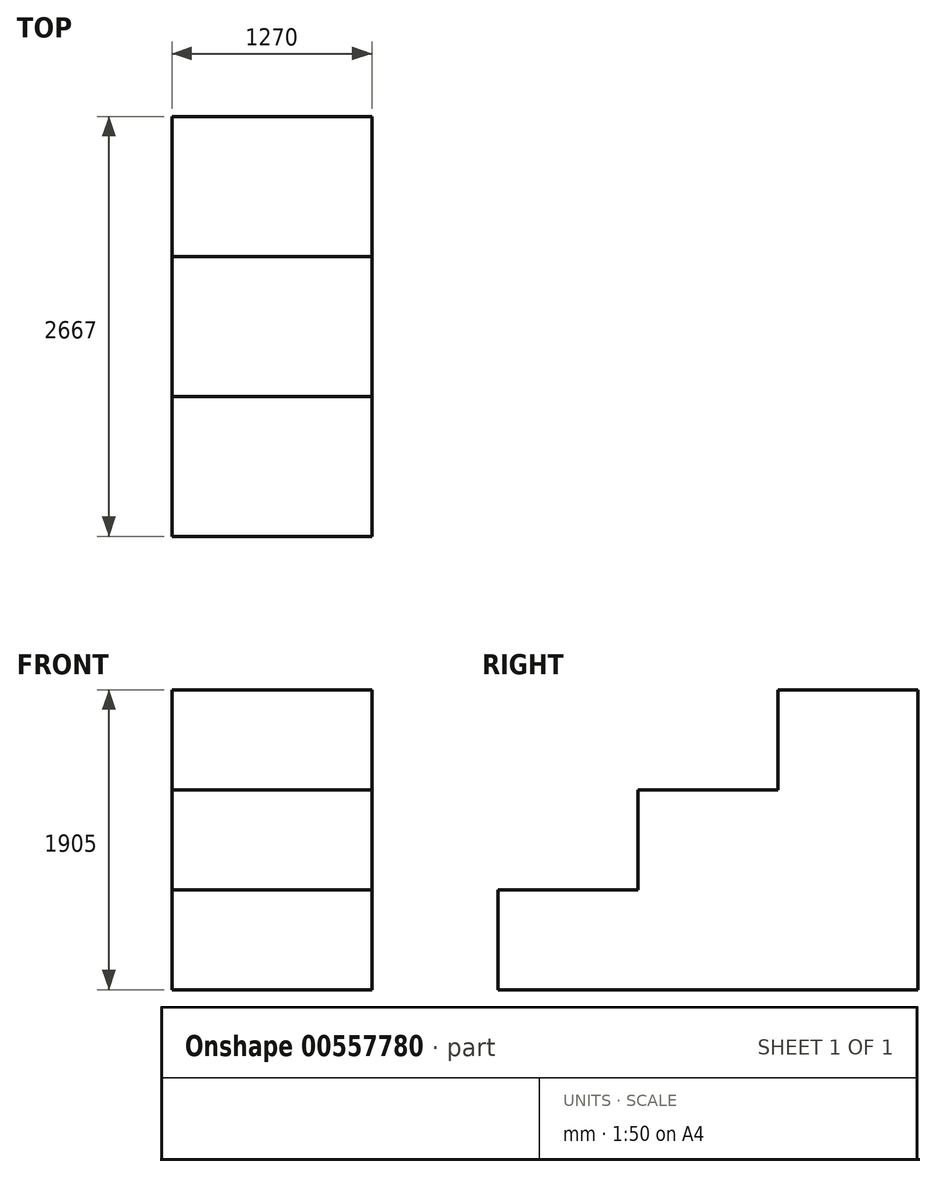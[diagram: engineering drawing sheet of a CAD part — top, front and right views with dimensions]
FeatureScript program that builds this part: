
annotation { "Feature Type Name" : "Feature", "Feature Type Description" : "" }
export const myFeature = defineFeature(function(context is Context, id is Id, definition is map)
    precondition{}
    {
        {
            var Q0;
            Q0=qCreatedBy(makeId("Right.planeOp"),FACE);
            var sketch = newSketch(context, id + "F0", { "sketchPlane" : qUnion([Q0])});
            skLineSegment(sketch, "E0", {"start": v(-65.9, -39.16) * mm, "end": v(2601.1, -39.16) * mm});
            skLineSegment(sketch, "E1", {"start": v(2601.1, -39.16) * mm, "end": v(2601.1, 1865.84) * mm});
            skLineSegment(sketch, "E2", {"start": v(2601.1, 1865.84) * mm, "end": v(1712.1, 1865.84) * mm});
            skLineSegment(sketch, "E3", {"start": v(1712.1, 1865.84) * mm, "end": v(1712.1, 1230.84) * mm});
            skLineSegment(sketch, "E4", {"start": v(1712.1, 1230.84) * mm, "end": v(823.1, 1230.84) * mm});
            skLineSegment(sketch, "E5", {"start": v(823.1, 1230.84) * mm, "end": v(823.1, 595.84) * mm});
            skLineSegment(sketch, "E6", {"start": v(823.1, 595.84) * mm, "end": v(-65.9, 595.84) * mm});
            skLineSegment(sketch, "E7", {"start": v(-65.9, 595.84) * mm, "end": v(-65.9, -39.16) * mm});
            skSolve(sketch);
        }
        {
            var Q0;
            Q0=makeQuery(id+"F0.imprint","IMPRINT",FACE,{"disambiguationData":[TD([[makeQuery(id+"F0.imprint","IMPRINT",EDGE,{"derivedFrom":sQuery(id+"F0.wireOp",EDGE,"E0")}),1.0]])]});
            extrude(context, id + "F1", {"entities" : qUnion([Q0]), "depth" : 1270 * mm, "offsetDistance" : 25.4 * mm});
        }
    });
